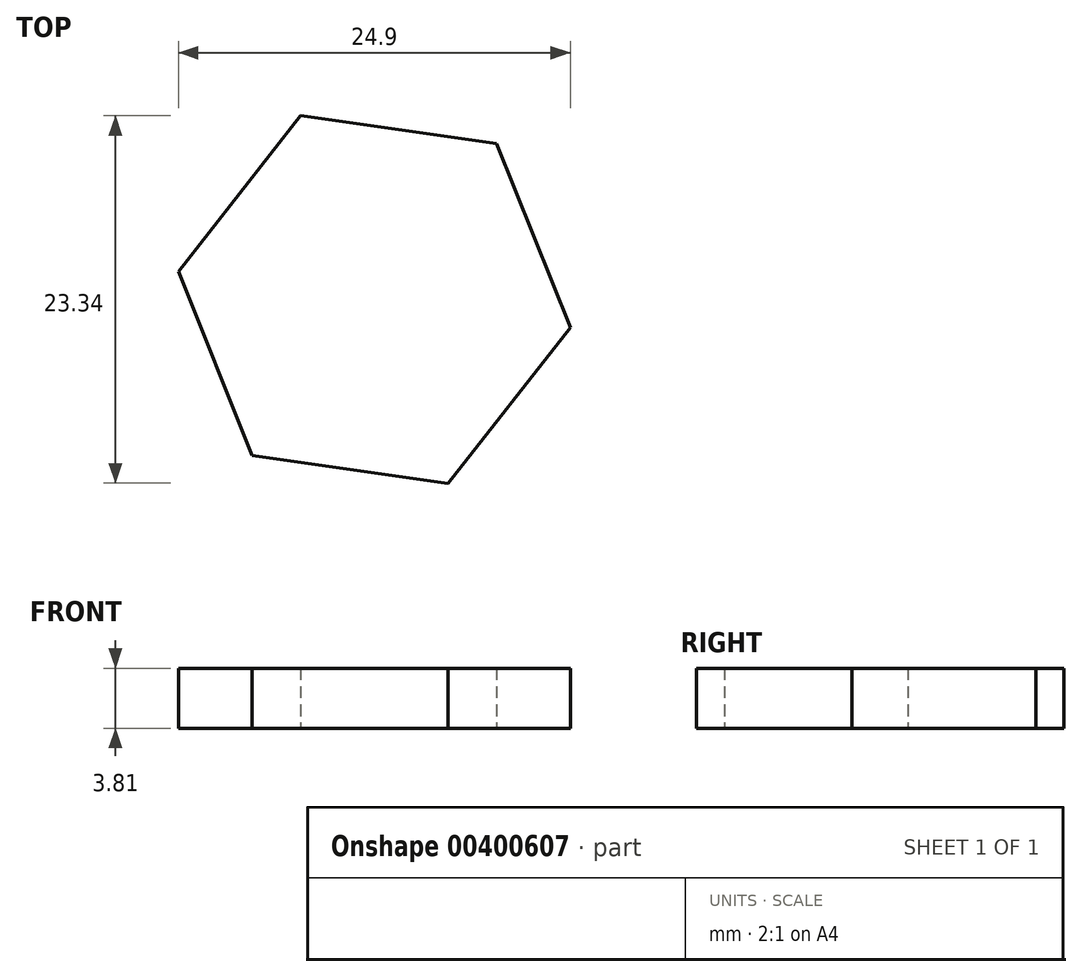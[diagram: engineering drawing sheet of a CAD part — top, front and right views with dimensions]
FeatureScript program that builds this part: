
annotation { "Feature Type Name" : "Feature", "Feature Type Description" : "" }
export const myFeature = defineFeature(function(context is Context, id is Id, definition is map)
    precondition{}
    {
        {
            var Q0;
            Q0=qCreatedBy(makeId("Top.planeOp"),FACE);
            var sketch = newSketch(context, id + "F0", { "sketchPlane" : qUnion([Q0])});
            skCircle(sketch, "E0.cCircle", {"center": v(-35.94, 39.95) * mm, "radius": 10.9 * mm, "construction": true});
            skLineSegment(sketch, "E0.0", {"start": v(-43.7, 30.05) * mm, "end": v(-48.39, 41.72) * mm});
            skLineSegment(sketch, "E0.1", {"start": v(-48.39, 41.72) * mm, "end": v(-40.62, 51.62) * mm});
            skLineSegment(sketch, "E0.2", {"start": v(-40.62, 51.62) * mm, "end": v(-28.17, 49.84) * mm});
            skLineSegment(sketch, "E0.3", {"start": v(-28.17, 49.84) * mm, "end": v(-23.5, 38.17) * mm});
            skLineSegment(sketch, "E0.4", {"start": v(-23.5, 38.17) * mm, "end": v(-31.25, 28.28) * mm});
            skLineSegment(sketch, "E0.5", {"start": v(-31.25, 28.28) * mm, "end": v(-43.7, 30.05) * mm});
            skPoint(sketch, "E0.0.midPoint", {"position": v(-46.05, 35.89) * mm});
            skSolve(sketch);
        }
        {
            var Q0;
            Q0 = qSketchRegion(id + "F0", true);
            extrude(context, id + "F1", {"entities" : qUnion([Q0]), "depth" : 3.8 * mm});
        }
    });
